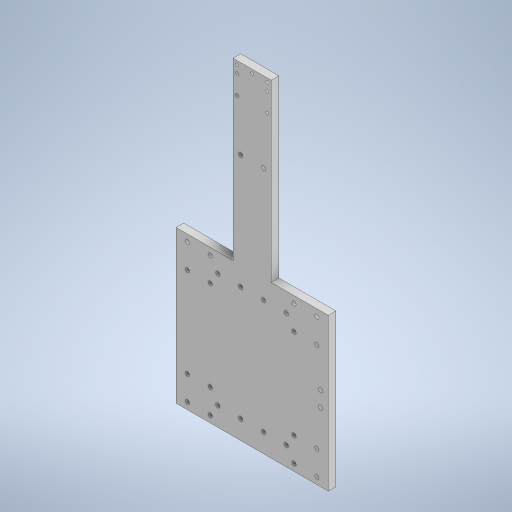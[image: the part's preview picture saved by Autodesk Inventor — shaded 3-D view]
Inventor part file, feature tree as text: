
AUTODESK INVENTOR PART (.ipt)
format: ipt  version: 2024 (Build 280153000, 153)  size: 364,032 bytes
history: native  units: mm
features: extrude x1, sketch x1
ambient origin geometry x8: Origin, YZ Plane, XZ Plane, XY Plane, X Axis, Y Axis, Z Axis, Center Point
bodies: Solido1 (feature_tree)
feature tree (2):
  extrude  "Estrusione1"  Depth=200.0mm
  sketch  "Schizzo1"
